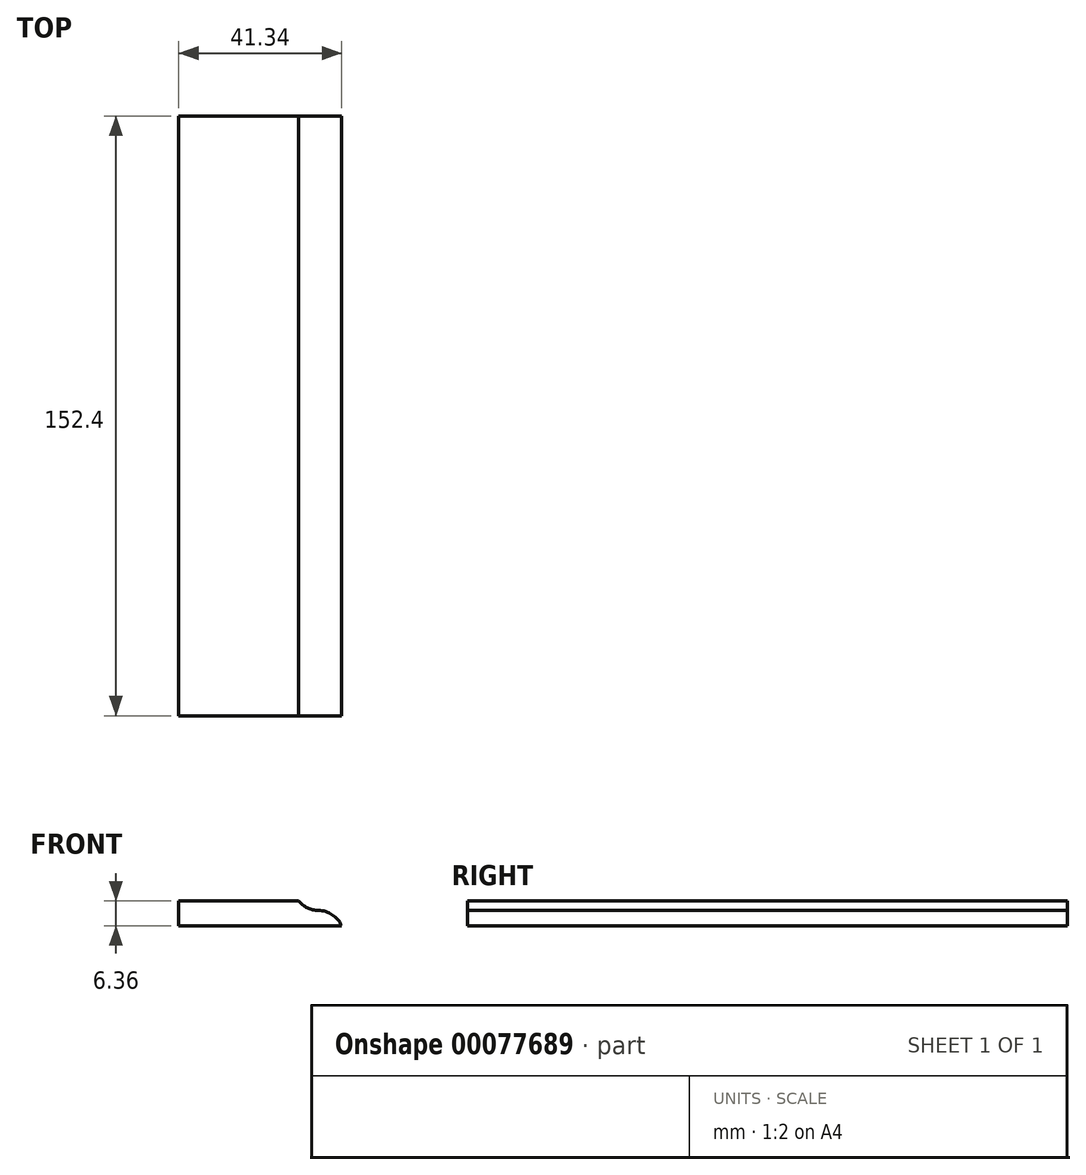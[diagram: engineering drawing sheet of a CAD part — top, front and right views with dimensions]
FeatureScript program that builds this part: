
annotation { "Feature Type Name" : "Feature", "Feature Type Description" : "" }
export const myFeature = defineFeature(function(context is Context, id is Id, definition is map)
    precondition{}
    {
        {
            var Q0;
            Q0=qCreatedBy(makeId("Front.planeOp"),FACE);
            var sketch = newSketch(context, id + "F0", { "sketchPlane" : qUnion([Q0])});
            skArc(sketch, "E0", {"start": v(9.79, 3.18) * mm, "mid": v(12, 1.38) * mm, "end": v(14.8, 0.74) * mm});
            skLineSegment(sketch, "E1", {"start": v(-20.67, 3.18) * mm, "end": v(9.79, 3.18) * mm});
            skArc(sketch, "E2", {"start": v(20.67, -3.18) * mm, "mid": v(18.32, -0.33) * mm, "end": v(14.8, 0.74) * mm});
            skLineSegment(sketch, "E3", {"start": v(-20.67, -3.18) * mm, "end": v(20.67, -3.18) * mm});
            skLineSegment(sketch, "E4", {"start": v(-20.67, 3.18) * mm, "end": v(-20.67, -3.18) * mm});
            skSolve(sketch);
        }
        {
            var Q0;
            Q0=makeQuery(id+"F0.imprint","IMPRINT",FACE,{"disambiguationData":[TD([[makeQuery(id+"F0.imprint","IMPRINT",EDGE,{"derivedFrom":sQuery(id+"F0.wireOp",EDGE,"E0")}),-1.0]])]});
            extrude(context, id + "F1", {"entities" : qUnion([Q0]), "depth" : 152.4 * mm});
        }
    });
